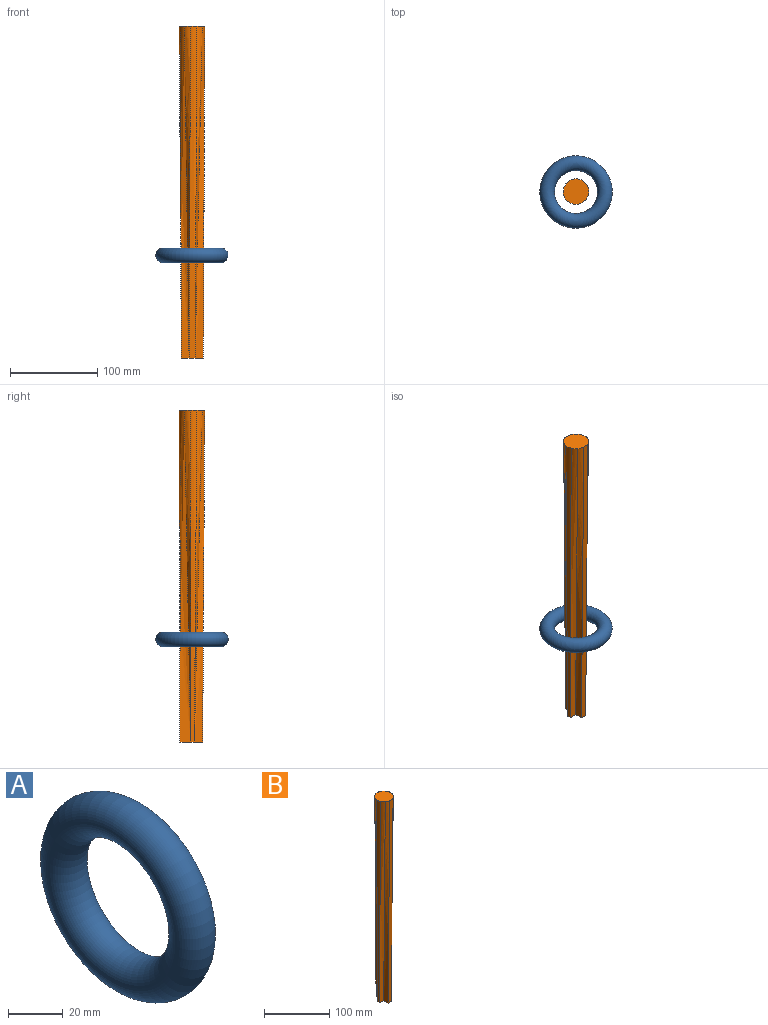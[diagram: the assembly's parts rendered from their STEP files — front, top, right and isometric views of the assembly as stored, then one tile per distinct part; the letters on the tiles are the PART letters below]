
ASSEMBLY  parts=2 mates=1
PART A: 1 faces, bbox 16.9x90x90 mm
  f0: torus R=33.11mm, axis (-1,0,0), area 11039.9mm2
PART B: 14 faces, bbox 29.3x29.3x381 mm
  f0: plane 26.17x25.31mm, normal (0,0,-1), area 257.4mm2, adj f2,f3,f4,f5,f6,f7,f8,f9
  f1: plane 29.2x29.2mm, normal (0,0,1), area 668.9mm2, adj f2,f3,f4,f5,f6,f7,f8,f9
  f2: bspline ~381x7.48mm, area 2251.8mm2, adj f0,f1,f3,f13
  f3: bspline ~381x10.06mm, area 2930.8mm2, adj f0,f1,f2,f4
  f4: bspline ~381x11.8mm, area 2917.7mm2, adj f0,f1,f3,f5
  f5: bspline ~381x9.05mm, area 2752.9mm2, adj f0,f1,f4,f6
  f6: bspline ~381x10.76mm, area 3060.9mm2, adj f0,f1,f5,f7
  f7: bspline ~381x11mm, area 2914.6mm2, adj f0,f1,f6,f8
  f8: bspline ~381x8.35mm, area 2251.8mm2, adj f0,f1,f7,f9
  f9: bspline ~381x10.1mm, area 3057.9mm2, adj f0,f1,f8,f10
  f10: bspline ~381x12.94mm, area 3400.8mm2, adj f0,f1,f9,f11
  f11: bspline ~381x9.15mm, area 2752.8mm2, adj f0,f1,f10,f12
  f12: bspline ~381x12.36mm, area 3560.9mm2, adj f0,f1,f11,f13
  f13: bspline ~381x11.1mm, area 2792.8mm2, adj f0,f1,f2,f12
PLACE A rot(axis=(0,-1,0),90deg) t=(89.11,-43.91,145.67)mm
PLACE B t=(142.77,-72.15,0)mm
MATE cylindrical A.f0 <-> B.f1  axis (0,0,-1) through (89.11,-59.87,117.78)mm
